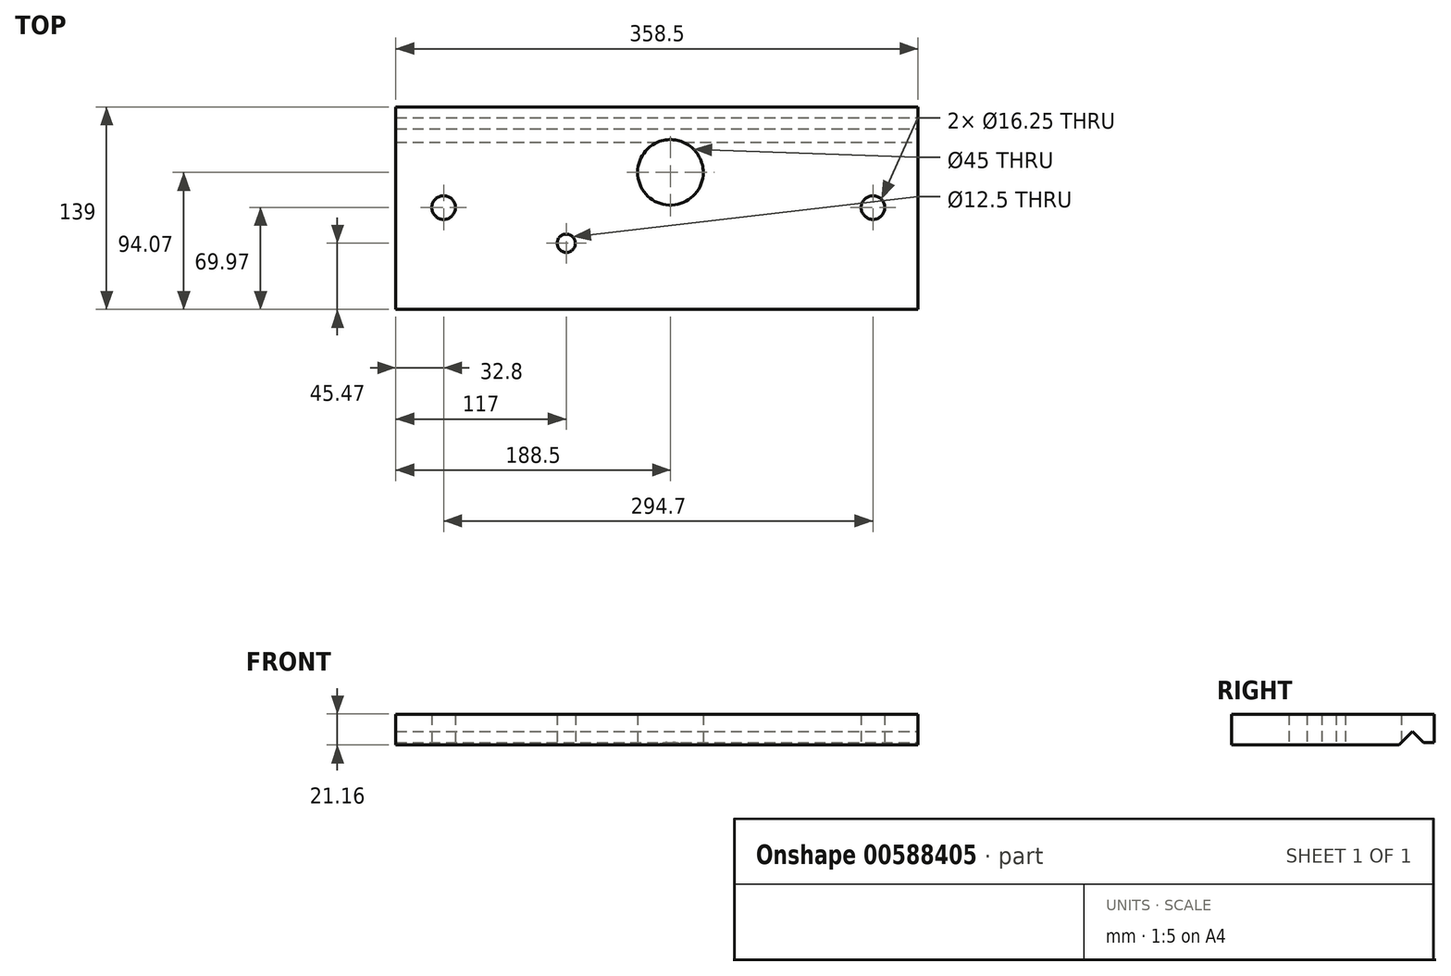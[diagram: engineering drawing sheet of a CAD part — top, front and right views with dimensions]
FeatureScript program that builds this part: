
annotation { "Feature Type Name" : "Feature", "Feature Type Description" : "" }
export const myFeature = defineFeature(function(context is Context, id is Id, definition is map)
    precondition{}
    {
        {
            var Q0;
            Q0=qCreatedBy(makeId("Top.planeOp"),FACE);
            var sketch = newSketch(context, id + "F0", { "sketchPlane" : qUnion([Q0])});
            skLineSegment(sketch, "E0.bottom", {"start": v(-179.25, -69.5) * mm, "end": v(179.25, -69.5) * mm});
            skLineSegment(sketch, "E0.top", {"start": v(-179.25, 69.5) * mm, "end": v(179.25, 69.5) * mm});
            skLineSegment(sketch, "E0.left", {"start": v(-179.25, -69.5) * mm, "end": v(-179.25, 69.5) * mm});
            skLineSegment(sketch, "E0.right", {"start": v(179.25, -69.5) * mm, "end": v(179.25, 69.5) * mm});
            skPoint(sketch, "E0.middle", {"position": v(0, 0) * mm});
            skSolve(sketch);
        }
        {
            var Q0;
            Q0 = qSketchRegion(id + "F0", true);
            extrude(context, id + "F1", {"entities" : qUnion([Q0]), "endBound" : BoundingType.SYMMETRIC, "depth" : 21.15 * mm, "offsetDistance" : 25 * mm});
        }
        {
            var Q0;
            Q0=makeQuery(id+"F1.opExtrude","SWEPT_FACE",FACE,{"disambiguationData":[OSD([sQuery(id+"F0.wireOp",EDGE,"E0.right")])]});
            var sketch = newSketch(context, id + "F2", { "sketchPlane" : qUnion([Q0])});
            skLineSegment(sketch, "E1", {"start": v(54.5, 10.58) * mm, "end": v(54.5, -10.57) * mm, "construction": true});
            skLineSegment(sketch, "E2", {"start": v(62.15, -8.97) * mm, "end": v(54.5, -1.33) * mm});
            skLineSegment(sketch, "E3", {"start": v(54.5, -1.32) * mm, "end": v(45.25, -10.58) * mm});
            skLineSegment(sketch, "E4", {"start": v(69.5, -8.97) * mm, "end": v(62.15, -8.97) * mm});
            skPoint(sketch, "E5.orphan", {"position": v(63.75, -10.58) * mm});
            skLineSegment(sketch, "E6", {"start": v(45.25, -10.58) * mm, "end": v(69.5, -10.58) * mm});
            skLineSegment(sketch, "E7", {"start": v(69.5, -10.58) * mm, "end": v(69.5, -8.97) * mm});
            skSolve(sketch);
        }
        {
            var Q0;
            Q0 = qSketchRegion(id + "F2", true);
            extrude(context, id + "F3", {"entities" : qUnion([Q0]), "operationType" : NewBodyOperationType.REMOVE, "endBound" : BoundingType.THROUGH_ALL, "oppositeDirection" : true, "depth" : 25 * mm, "offsetDistance" : 25 * mm});
        }
        {
            var Q0;
            Q0=makeQuery(id+"F1.opExtrude","CAP_FACE",FACE,{"disambiguationData":[OSD([sQuery(id+"F0.wireOp",EDGE,"E0.bottom"),sQuery(id+"F0.wireOp",EDGE,"E0.top"),sQuery(id+"F0.wireOp",EDGE,"E0.left"),sQuery(id+"F0.wireOp",EDGE,"E0.right")])],"isStart":true});
            var sketch = newSketch(context, id + "F4", { "sketchPlane" : qUnion([Q0])});
            skCircle(sketch, "E8", {"center": v(148.25, -0.47) * mm, "radius": 8.12 * mm});
            skLineSegment(sketch, "E9", {"start": v(173.4, -44.97) * mm, "end": v(-166.6, -44.97) * mm, "construction": true});
            skCircle(sketch, "E10", {"center": v(-146.45, -0.47) * mm, "radius": 8.12 * mm});
            skCircle(sketch, "E11", {"center": v(-62.25, 24.03) * mm, "radius": 6.25 * mm});
            skCircle(sketch, "E12", {"center": v(9.25, -24.57) * mm, "radius": 22.5 * mm});
            skSolve(sketch);
        }
        {
            var Q0;
            Q0 = qSketchRegion(id + "F4", true);
            extrude(context, id + "F5", {"entities" : qUnion([Q0]), "operationType" : NewBodyOperationType.REMOVE, "endBound" : BoundingType.THROUGH_ALL, "oppositeDirection" : true, "depth" : 25 * mm, "offsetDistance" : 25 * mm});
        }
    });
